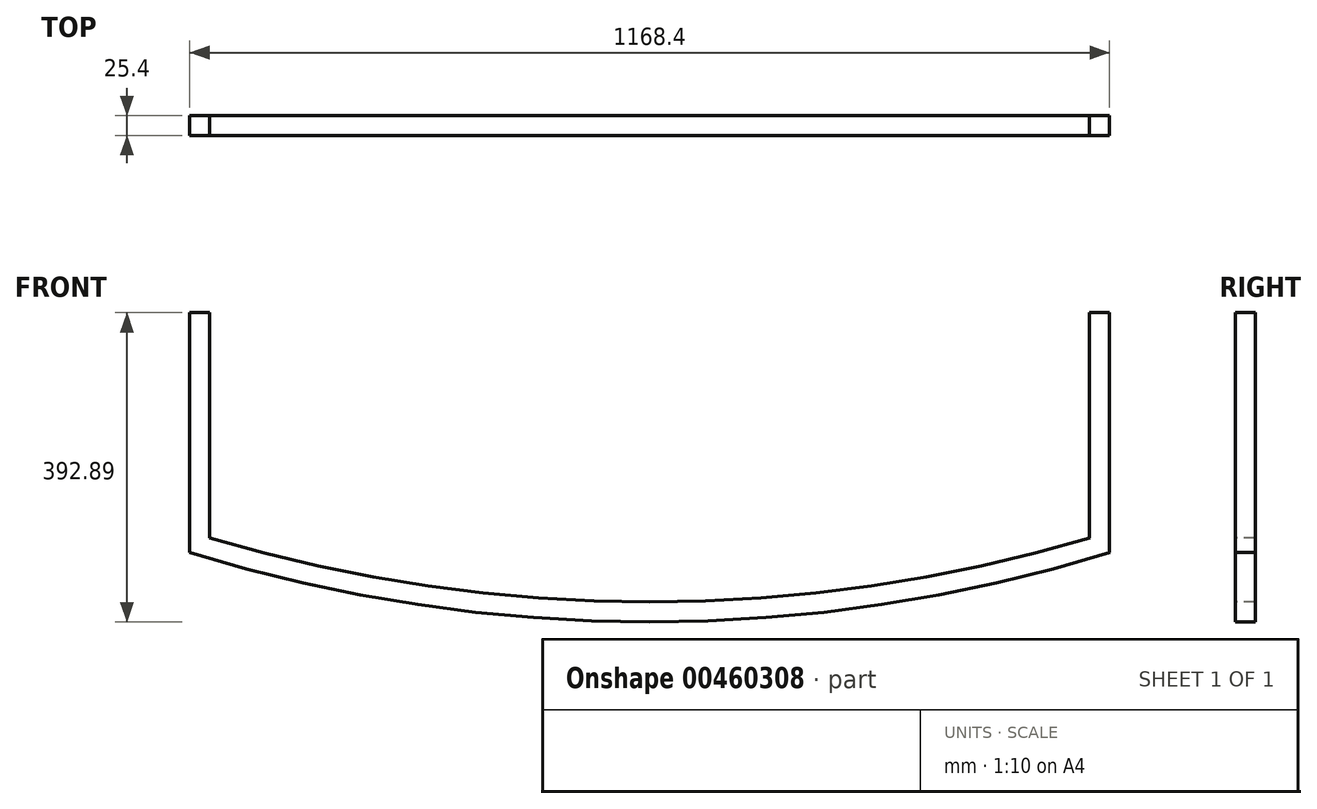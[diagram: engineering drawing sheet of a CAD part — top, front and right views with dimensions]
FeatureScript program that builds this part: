
annotation { "Feature Type Name" : "Feature", "Feature Type Description" : "" }
export const myFeature = defineFeature(function(context is Context, id is Id, definition is map)
    precondition{}
    {
        {
            var Q0;
            Q0=qCreatedBy(makeId("Front.planeOp"),FACE);
            var sketch = newSketch(context, id + "F0", { "sketchPlane" : qUnion([Q0])});
            skLineSegment(sketch, "E0.bottom", {"start": v(-584.2, 152.4) * mm, "end": v(584.2, 152.4) * mm});
            skLineSegment(sketch, "E0.left", {"start": v(-584.2, 152.4) * mm, "end": v(-584.2, -152.4) * mm});
            skLineSegment(sketch, "E0.right", {"start": v(584.2, 152.4) * mm, "end": v(584.2, -152.4) * mm});
            skArc(sketch, "E1", {"start": v(-584.2, -152.4) * mm, "mid": v(0, -240.5) * mm, "end": v(584.2, -152.4) * mm});
            skSolve(sketch);
        }
        {
            var Q0;
            Q0=qSketchRegion(id+"F0",true);
            extrude(context, id + "F1", {"entities" : qUnion([Q0]), "depth" : 25.4 * mm});
        }
        {
            var Q0;
            Q0=makeQuery(id+"F1.opExtrude","CAP_FACE",FACE,{"disambiguationData":[OSD([sQuery(id+"F0.wireOp",EDGE,"E0.bottom"),sQuery(id+"F0.wireOp",EDGE,"E0.left"),sQuery(id+"F0.wireOp",EDGE,"E0.right"),sQuery(id+"F0.wireOp",EDGE,"E1")])],"isStart":false});
            var sketch = newSketch(context, id + "F2", { "sketchPlane" : qUnion([Q0])});
            skLineSegment(sketch, "E2.0", {"start": v(558.8, 152.4) * mm, "end": v(558.8, -133.56) * mm});
            skArc(sketch, "E2.1", {"start": v(-558.8, -133.56) * mm, "mid": v(0, -215.1) * mm, "end": v(558.8, -133.56) * mm});
            skLineSegment(sketch, "E2.2", {"start": v(-558.8, 152.4) * mm, "end": v(-558.8, -133.56) * mm});
            skLineSegment(sketch, "E3", {"start": v(-558.8, 152.4) * mm, "end": v(558.8, 152.4) * mm});
            skSolve(sketch);
        }
        {
            var Q0;
            Q0 = qSketchRegion(id + "F2", true);
            extrude(context, id + "F3", {"entities" : qUnion([Q0]), "operationType" : NewBodyOperationType.REMOVE, "endBound" : BoundingType.THROUGH_ALL, "oppositeDirection" : true, "depth" : 25.4 * mm});
        }
    });
